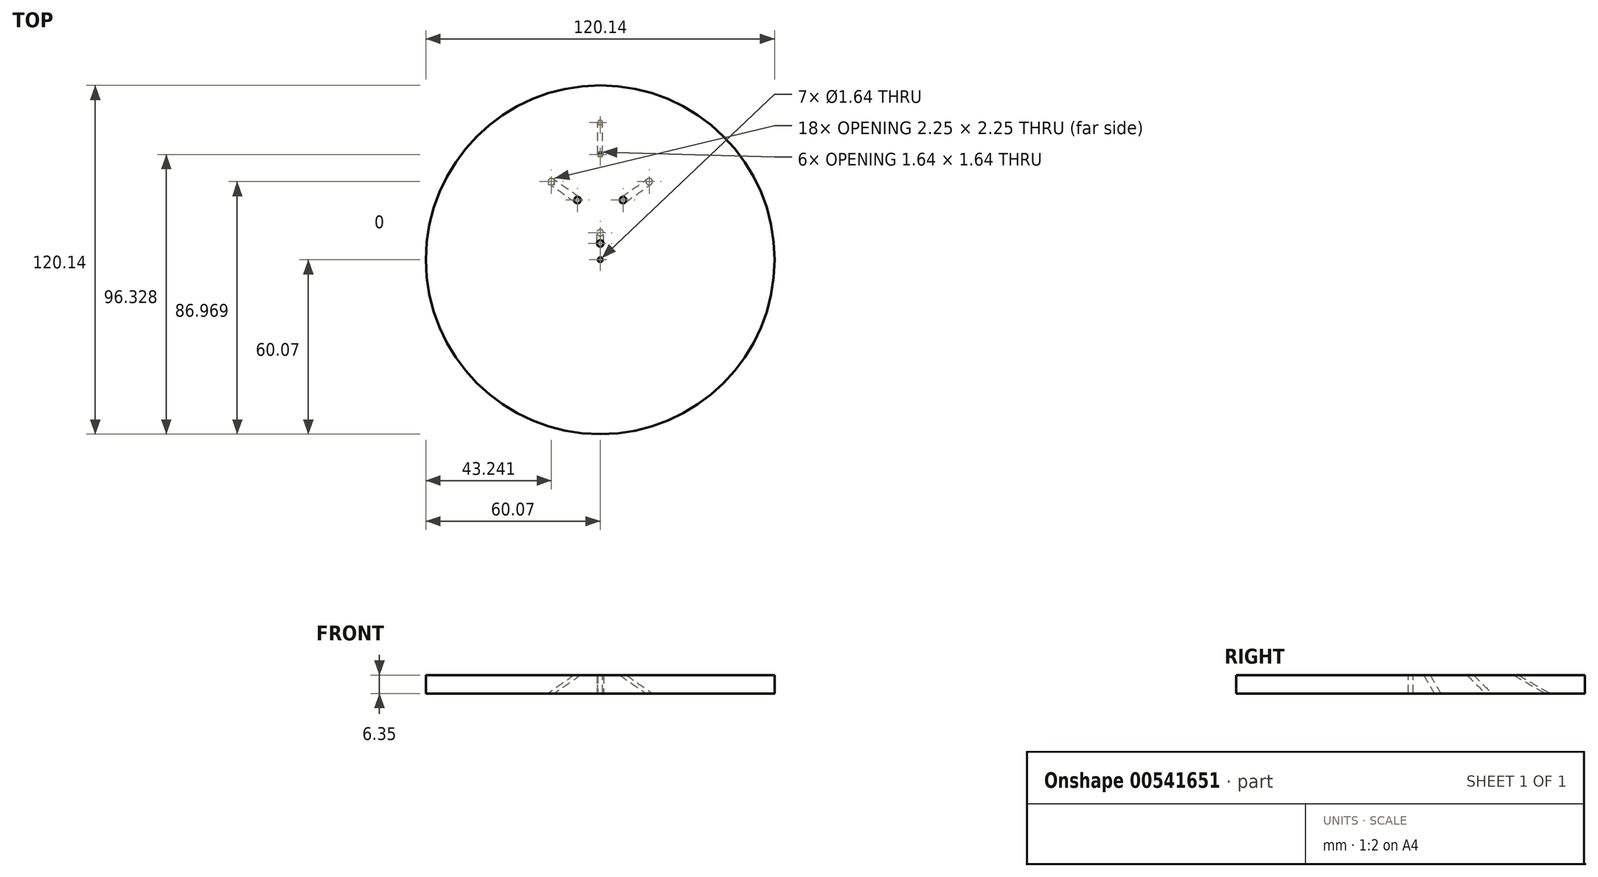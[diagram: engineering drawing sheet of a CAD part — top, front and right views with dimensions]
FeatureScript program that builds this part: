
annotation { "Feature Type Name" : "Feature", "Feature Type Description" : "" }
export const myFeature = defineFeature(function(context is Context, id is Id, definition is map)
    precondition{}
    {
        {
            var Q0;
            Q0=qCreatedBy(makeId("Top.planeOp"),FACE);
            var sketch = newSketch(context, id + "F0", { "sketchPlane" : qUnion([Q0])});
            skCircle(sketch, "E0", {"center": v(0, 0) * mm, "radius": 60.07 * mm});
            skSolve(sketch);
        }
        {
            var Q0;
            Q0=qCreatedBy(makeId("Top.planeOp"),FACE);
            var sketch = newSketch(context, id + "F1", { "sketchPlane" : qUnion([Q0])});
            skCircle(sketch, "E1", {"center": v(0, 0) * mm, "radius": 0.82 * mm});
            skCircle(sketch, "E2", {"center": v(0, 5.61) * mm, "radius": 1.12 * mm});
            skCircle(sketch, "E3", {"center": v(0, 36.26) * mm, "radius": 0.82 * mm});
            skCircle(sketch, "E4", {"center": v(-7.85, 20.55) * mm, "radius": 1.12 * mm});
            skCircle(sketch, "E5", {"center": v(7.85, 20.55) * mm, "radius": 1.12 * mm});
            skLineSegment(sketch, "E6", {"start": v(7.85, 20.55) * mm, "end": v(-7.85, 20.55) * mm, "construction": true});
            skSolve(sketch);
        }
        {
            var Q0;
            Q0=sQuery(id+"F1.wireOp",EDGE,"E6");
            cPlane(context, id + "F2", {"entities" : qUnion([Q0]), "cplaneType" : CPlaneType.LINE_ANGLE, "offset" : 25.4 * mm, "angle" : 45 * degree, "oppositeDirection" : true, "width" : 152.4 * mm, "height" : 152.4 * mm});
        }
        {
            var Q0;
            Q0=qCreatedBy(makeId("Top.planeOp"),FACE);
            var sketch = newSketch(context, id + "F3", { "sketchPlane" : qUnion([Q0])});
            skCircle(sketch, "E7.0", {"center": v(0, 0) * mm, "radius": 0.82 * mm});
            skSolve(sketch);
        }
        {
            var Q0;
            Q0=makeQuery(id+"F0.imprint","IMPRINT",FACE,{"disambiguationData":[TD([[makeQuery(id+"F0.imprint","IMPRINT",EDGE,{"derivedFrom":sQuery(id+"F0.wireOp",EDGE,"E0")}),1.0]])]});
            var sketch = newSketch(context, id + "F4", { "sketchPlane" : qUnion([Q0])});
            skCircle(sketch, "E8.0", {"center": v(0, 5.61) * mm, "radius": 1.12 * mm});
            skSolve(sketch);
        }
        {
            var Q0;
            Q0=qCreatedBy(makeId("Right.planeOp"),FACE);
            var sketch = newSketch(context, id + "F5", { "sketchPlane" : qUnion([Q0])});
            skLineSegment(sketch, "E9", {"start": v(5.61, 0) * mm, "end": v(-248.39, 439.94) * mm});
            skLineSegment(sketch, "E10", {"start": v(5.61, 0) * mm, "end": v(259.61, -439.94) * mm});
            skSolve(sketch);
        }
        {
            var Q0;
            Q0=qCreatedBy(makeId("Top.planeOp"),FACE);
            var sketch = newSketch(context, id + "F6", { "sketchPlane" : qUnion([Q0])});
            skCircle(sketch, "E11.0", {"center": v(7.85, 20.55) * mm, "radius": 1.12 * mm});
            skSolve(sketch);
        }
        {
            var Q0;
            Q0=qCreatedBy(id+"F2.planeOp",FACE);
            var sketch = newSketch(context, id + "F7", { "sketchPlane" : qUnion([Q0])});
            skLineSegment(sketch, "E12", {"start": v(7.85, -14.53) * mm, "end": v(-351.88, 344.16) * mm});
            skLineSegment(sketch, "E13", {"start": v(7.85, -14.53) * mm, "end": v(245.65, -251.64) * mm});
            skSolve(sketch);
        }
        {
            var Q0;
            Q0=qCreatedBy(makeId("Top.planeOp"),FACE);
            var sketch = newSketch(context, id + "F8", { "sketchPlane" : qUnion([Q0])});
            skCircle(sketch, "E14.0", {"center": v(-7.85, 20.55) * mm, "radius": 1.12 * mm});
            skSolve(sketch);
        }
        {
            var Q0;
            Q0=qCreatedBy(id+"F2.planeOp",FACE);
            var sketch = newSketch(context, id + "F9", { "sketchPlane" : qUnion([Q0])});
            skLineSegment(sketch, "E15", {"start": v(-7.85, -14.53) * mm, "end": v(351.36, 344.68) * mm});
            skLineSegment(sketch, "E16", {"start": v(-7.85, -14.53) * mm, "end": v(-367.06, -373.74) * mm});
            skSolve(sketch);
        }
        {
            var Q0;
            Q0=qCreatedBy(makeId("Top.planeOp"),FACE);
            var sketch = newSketch(context, id + "F10", { "sketchPlane" : qUnion([Q0])});
            skCircle(sketch, "E17.0", {"center": v(0, 36.26) * mm, "radius": 0.82 * mm});
            skSolve(sketch);
        }
        {
            var Q0;
            Q0=qCreatedBy(makeId("Right.planeOp"),FACE);
            var sketch = newSketch(context, id + "F11", { "sketchPlane" : qUnion([Q0])});
            skLineSegment(sketch, "E18", {"start": v(36.26, 0) * mm, "end": v(-403.68, 254) * mm});
            skLineSegment(sketch, "E19", {"start": v(36.26, 0) * mm, "end": v(476.2, -254) * mm});
            skSolve(sketch);
        }
        {
            var Q0;
            Q0 = qSketchRegion(id + "F0", true);
            extrude(context, id + "F12", {"entities" : qUnion([Q0]), "oppositeDirection" : true, "depth" : 6.35 * mm, "offsetDistance" : 25.4 * mm});
        }
        {
            var Q0;
            Q0 = qSketchRegion(id + "F3", true);
            extrude(context, id + "F13", {"entities" : qUnion([Q0]), "operationType" : NewBodyOperationType.REMOVE, "endBound" : BoundingType.THROUGH_ALL, "oppositeDirection" : true, "depth" : 25.4 * mm, "offsetDistance" : 25.4 * mm});
        }
        {
            var Q0;
            Q0 = qSketchRegion(id + "F4", true);
            var Q1;
            Q1=sQuery(id+"F5.wireOp",EDGE,"E10");
            sweep(context, id + "F14", {"operationType" : NewBodyOperationType.REMOVE, "profiles" : qUnion([Q0]), "path" : qUnion([Q1])});
        }
        {
            var Q0;
            Q0 = qSketchRegion(id + "F6", true);
            var Q1;
            Q1=sQuery(id+"F7.wireOp",EDGE,"E13");
            sweep(context, id + "F15", {"operationType" : NewBodyOperationType.REMOVE, "profiles" : qUnion([Q0]), "path" : qUnion([Q1])});
        }
        {
            var Q0;
            Q0 = qSketchRegion(id + "F8", true);
            var Q1;
            Q1=sQuery(id+"F9.wireOp",EDGE,"E16");
            sweep(context, id + "F16", {"operationType" : NewBodyOperationType.REMOVE, "profiles" : qUnion([Q0]), "path" : qUnion([Q1])});
        }
        {
            var Q0;
            Q0=makeQuery(id+"F10.imprint","IMPRINT",FACE,{"disambiguationData":[TD([[makeQuery(id+"F10.imprint","IMPRINT",EDGE,{"derivedFrom":sQuery(id+"F10.wireOp",EDGE,"E17.0")}),1.0]])]});
            var Q1;
            Q1=sQuery(id+"F11.wireOp",EDGE,"E19");
            sweep(context, id + "F17", {"operationType" : NewBodyOperationType.REMOVE, "profiles" : qUnion([Q0]), "path" : qUnion([Q1])});
        }
    });
